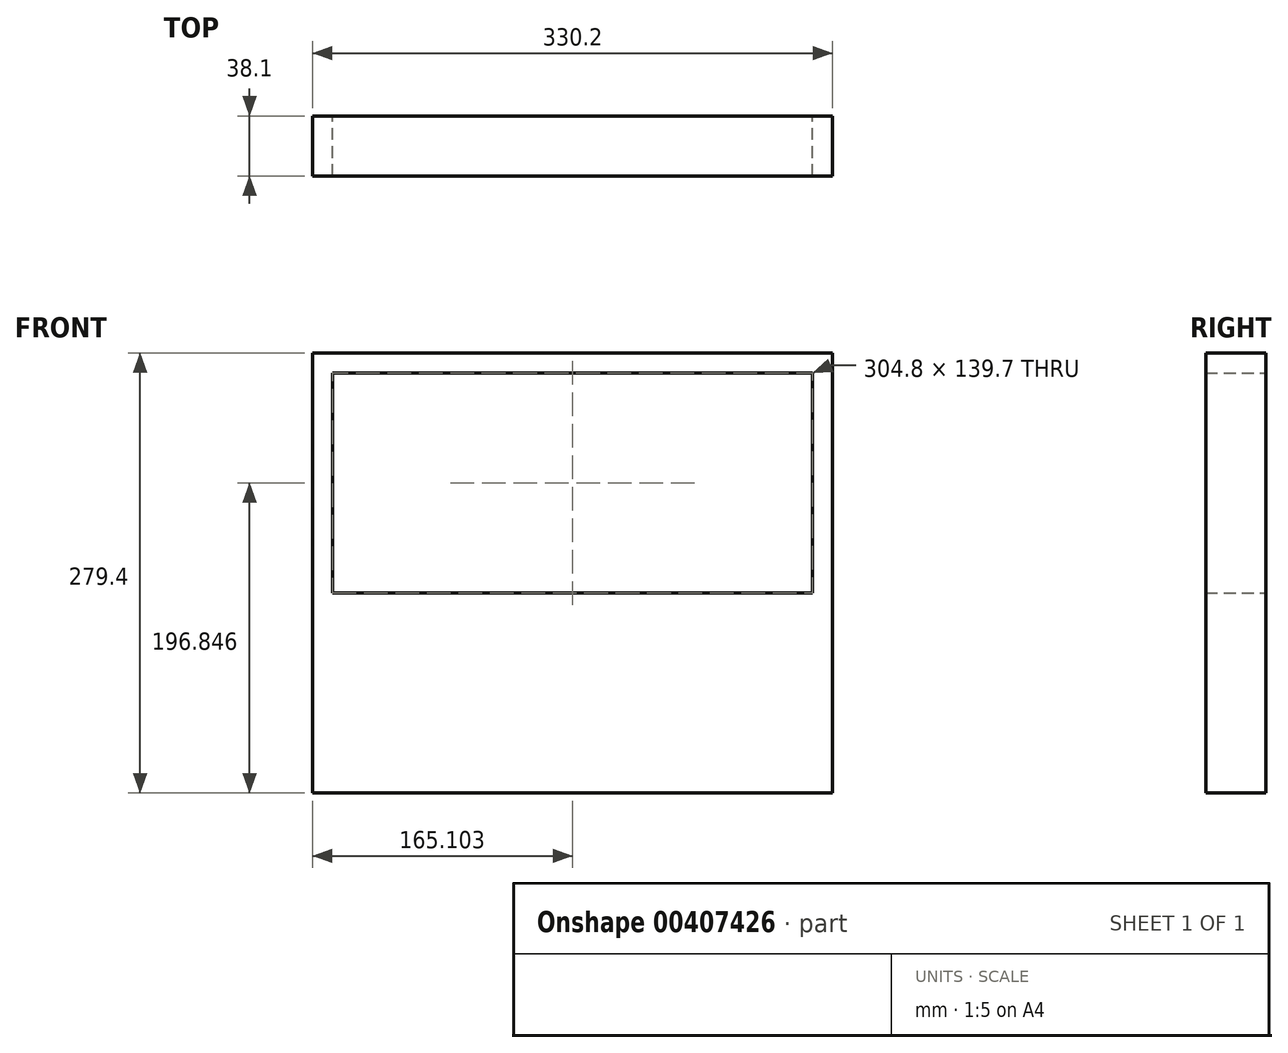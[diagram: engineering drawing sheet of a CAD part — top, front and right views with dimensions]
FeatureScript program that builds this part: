
annotation { "Feature Type Name" : "Feature", "Feature Type Description" : "" }
export const myFeature = defineFeature(function(context is Context, id is Id, definition is map)
    precondition{}
    {
        {
            var Q0;
            Q0=qCreatedBy(makeId("Front.planeOp"),FACE);
            var sketch = newSketch(context, id + "F0", { "sketchPlane" : qUnion([Q0])});
            skLineSegment(sketch, "E0.bottom", {"start": v(-76.04, 128.83) * mm, "end": v(-63.34, 128.83) * mm});
            skLineSegment(sketch, "E0.top", {"start": v(-76.04, -23.57) * mm, "end": v(-63.34, -23.57) * mm});
            skLineSegment(sketch, "E0.left", {"start": v(-76.04, 128.83) * mm, "end": v(-76.04, -23.57) * mm});
            skLineSegment(sketch, "E0.right", {"start": v(-63.34, 128.83) * mm, "end": v(-63.34, -23.57) * mm});
            skLineSegment(sketch, "E1.bottom", {"start": v(-63.34, 128.83) * mm, "end": v(241.46, 128.83) * mm});
            skLineSegment(sketch, "E1.top", {"start": v(-63.34, 116.13) * mm, "end": v(241.46, 116.13) * mm});
            skLineSegment(sketch, "E1.left", {"start": v(-63.34, 128.83) * mm, "end": v(-63.34, 116.13) * mm});
            skLineSegment(sketch, "E1.right", {"start": v(241.46, 128.83) * mm, "end": v(241.46, 116.13) * mm});
            skPoint(sketch, "E2.endSnap0", {"position": v(89.06, 116.13) * mm});
            skLineSegment(sketch, "E3.bottom", {"start": v(-76.04, -23.57) * mm, "end": v(254.16, -23.57) * mm});
            skLineSegment(sketch, "E3.top", {"start": v(-76.04, -150.57) * mm, "end": v(254.16, -150.57) * mm});
            skLineSegment(sketch, "E3.left", {"start": v(-76.04, -23.57) * mm, "end": v(-76.04, -150.57) * mm});
            skLineSegment(sketch, "E3.right", {"start": v(254.16, -23.57) * mm, "end": v(254.16, -150.57) * mm});
            skLineSegment(sketch, "E4.bottom", {"start": v(241.46, 128.83) * mm, "end": v(254.16, 128.83) * mm});
            skLineSegment(sketch, "E4.top", {"start": v(241.46, -23.57) * mm, "end": v(254.16, -23.57) * mm});
            skLineSegment(sketch, "E4.left", {"start": v(241.46, 128.83) * mm, "end": v(241.46, -23.57) * mm});
            skLineSegment(sketch, "E4.right", {"start": v(254.16, 128.83) * mm, "end": v(254.16, -23.57) * mm});
            skSolve(sketch);
        }
        {
            var Q0;
            {var subQ3=sQuery(id+"F0.wireOp",EDGE,"E4.bottom");Q0=makeQuery(id+"F0.imprint","IMPRINT",FACE,{"disambiguationData":[TD([[makeQuery(id+"F0.imprint","IMPRINT",EDGE,{"derivedFrom":subQ3}),-1.0]])]});}
            var Q1;
            Q1=makeQuery(id+"F0.imprint","IMPRINT",FACE,{"disambiguationData":[TD([[makeQuery(id+"F0.imprint","IMPRINT",EDGE,{"derivedFrom":sQuery(id+"F0.wireOp",EDGE,"E3.top")}),1.0]])]});
            var Q2;
            {var subQ0=sQuery(id+"F0.wireOp",EDGE,"E1.bottom");Q2=makeQuery(id+"F0.imprint","IMPRINT",FACE,{"disambiguationData":[TD([[makeQuery(id+"F0.imprint","IMPRINT",EDGE,{"derivedFrom":subQ0}),-1.0]])]});}
            var Q3;
            Q3=makeQuery(id+"F0.imprint","IMPRINT",FACE,{"disambiguationData":[TD([[makeQuery(id+"F0.imprint","IMPRINT",EDGE,{"derivedFrom":sQuery(id+"F0.wireOp",EDGE,"E0.bottom")}),-1.0]])]});
            extrude(context, id + "F1", {"entities" : qUnion([Q0, Q1, Q2, Q3]), "depth" : 38.1 * mm});
        }
    });
